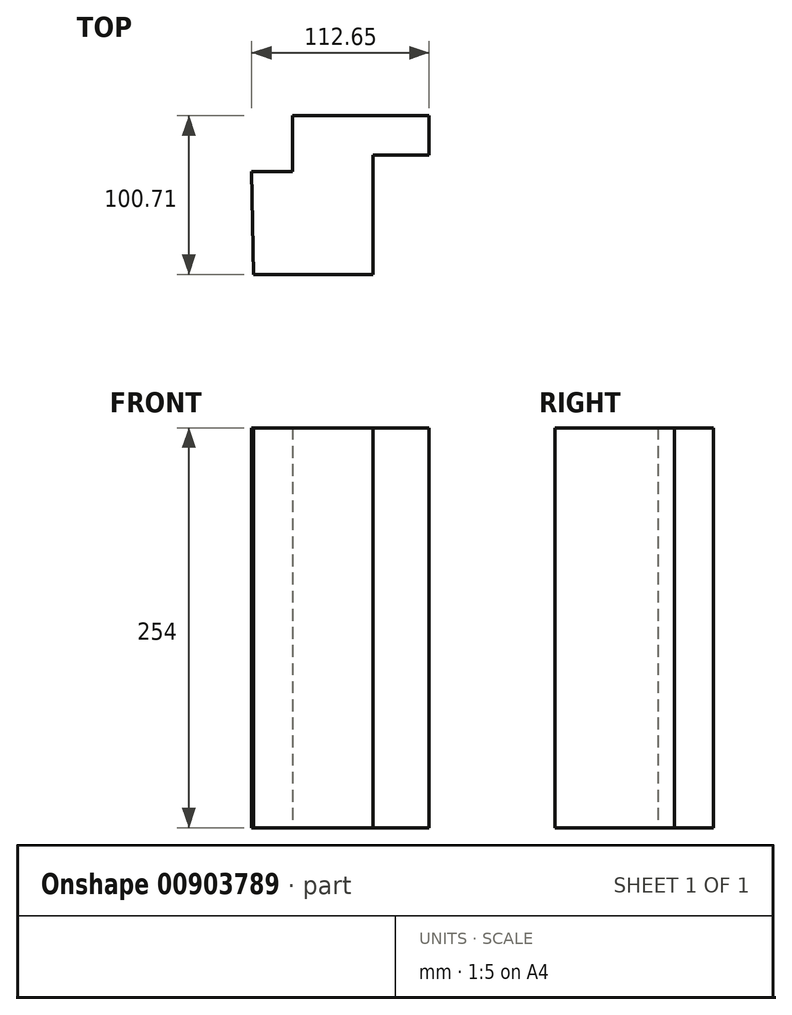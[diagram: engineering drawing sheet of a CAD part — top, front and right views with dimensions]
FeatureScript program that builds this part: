
annotation { "Feature Type Name" : "Feature", "Feature Type Description" : "" }
export const myFeature = defineFeature(function(context is Context, id is Id, definition is map)
    precondition{}
    {
        {
            var Q0;
            Q0=qCreatedBy(makeId("Top.planeOp"),FACE);
            var sketch = newSketch(context, id + "F0", { "sketchPlane" : qUnion([Q0])});
            skLineSegment(sketch, "E0", {"start": v(-75.83, -75.83) * mm, "end": v(0, -75.83) * mm});
            skLineSegment(sketch, "E1", {"start": v(0, -75.83) * mm, "end": v(0, 0) * mm});
            skLineSegment(sketch, "E2", {"start": v(0, 0) * mm, "end": v(35.63, 0) * mm});
            skLineSegment(sketch, "E3", {"start": v(35.63, 0) * mm, "end": v(35.63, 24.88) * mm});
            skLineSegment(sketch, "E4", {"start": v(35.63, 24.88) * mm, "end": v(-51.15, 24.88) * mm});
            skLineSegment(sketch, "E5", {"start": v(-51.15, 24.88) * mm, "end": v(-51.15, -10.55) * mm});
            skLineSegment(sketch, "E6", {"start": v(-51.15, -10.55) * mm, "end": v(-77.02, -10.55) * mm});
            skLineSegment(sketch, "E7", {"start": v(-77.02, -10.55) * mm, "end": v(-75.83, -75.83) * mm});
            skSolve(sketch);
        }
        {
            var Q0;
            Q0=makeQuery(id+"F0.imprint","IMPRINT",FACE,{"disambiguationData":[TD([[makeQuery(id+"F0.imprint","IMPRINT",EDGE,{"derivedFrom":sQuery(id+"F0.wireOp",EDGE,"E0")}),1.0]])]});
            extrude(context, id + "F1", {"entities" : qUnion([Q0]), "depth" : 254 * mm, "offsetDistance" : 25.4 * mm});
        }
    });
